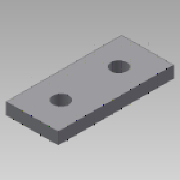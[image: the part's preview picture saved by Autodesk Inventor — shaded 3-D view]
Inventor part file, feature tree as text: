
AUTODESK INVENTOR PART (.ipt)
format: ipt  version: 2013 (Build 170138000, 138)  size: 94,208 bytes
history: native  units: mm
features: extrude x1, sketch x1
ambient origin geometry x8: Origin, YZ Plane, XZ Plane, XY Plane, X Axis, Y Axis, Z Axis, Center Point
bodies: Solid1 (feature_tree)
feature tree (2):
  extrude  "Extrusion1"  Depth=40.0mm
  sketch  "Sketch1"  dims[d0=18.0mm d2=40.0mm d3=5.3mm d4=10.0mm d5=9.0mm d6=4.0mm d7=0.0mm]
